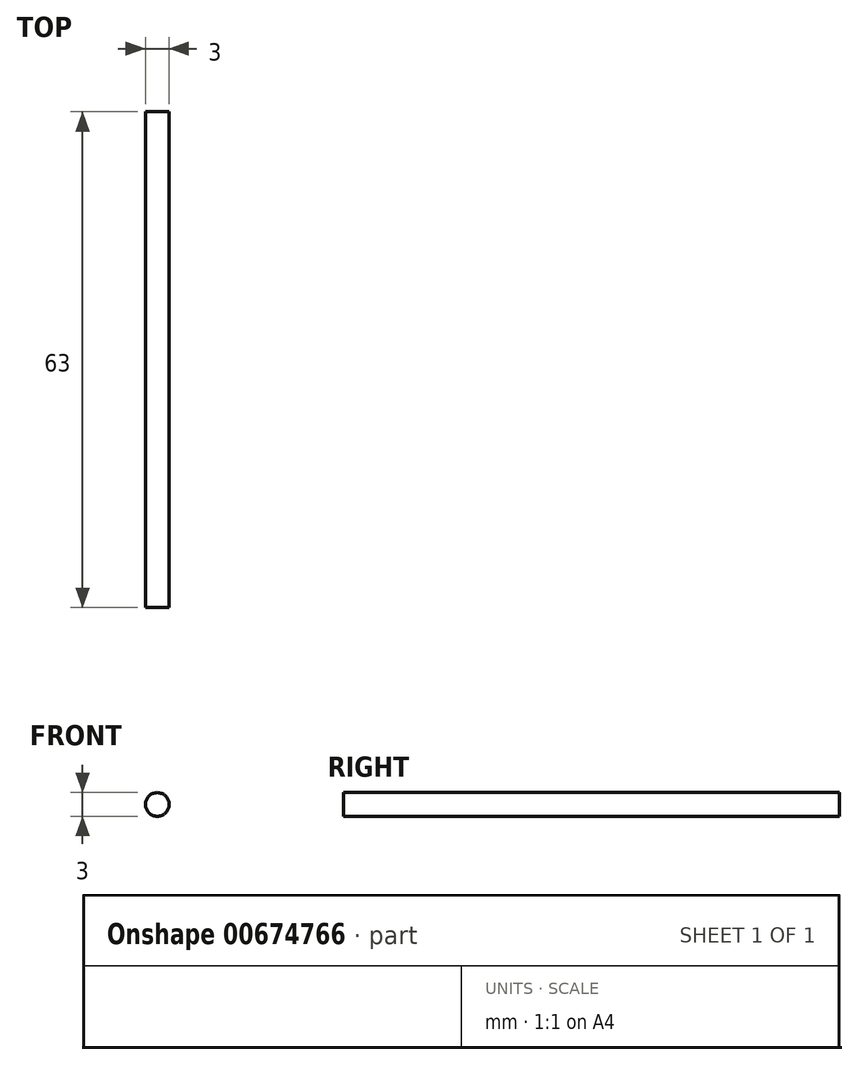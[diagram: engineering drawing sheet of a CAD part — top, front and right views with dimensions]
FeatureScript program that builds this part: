
annotation { "Feature Type Name" : "Feature", "Feature Type Description" : "" }
export const myFeature = defineFeature(function(context is Context, id is Id, definition is map)
    precondition{}
    {
        {
            var Q0;
            Q0=qCreatedBy(makeId("Front.planeOp"),FACE);
            var sketch = newSketch(context, id + "F0", { "sketchPlane" : qUnion([Q0])});
            skCircle(sketch, "E0", {"center": v(0, 0) * mm, "radius": 1.5 * mm});
            skSolve(sketch);
        }
        {
            var Q0;
            Q0=makeQuery(id+"F0.imprint","IMPRINT",FACE,{"disambiguationData":[TD([[makeQuery(id+"F0.imprint","IMPRINT",EDGE,{"derivedFrom":sQuery(id+"F0.wireOp",EDGE,"E0")}),1.0]])]});
            extrude(context, id + "F1", {"entities" : qUnion([Q0]), "oppositeDirection" : true, "depth" : 63 * mm, "offsetDistance" : 25 * mm});
        }
    });
